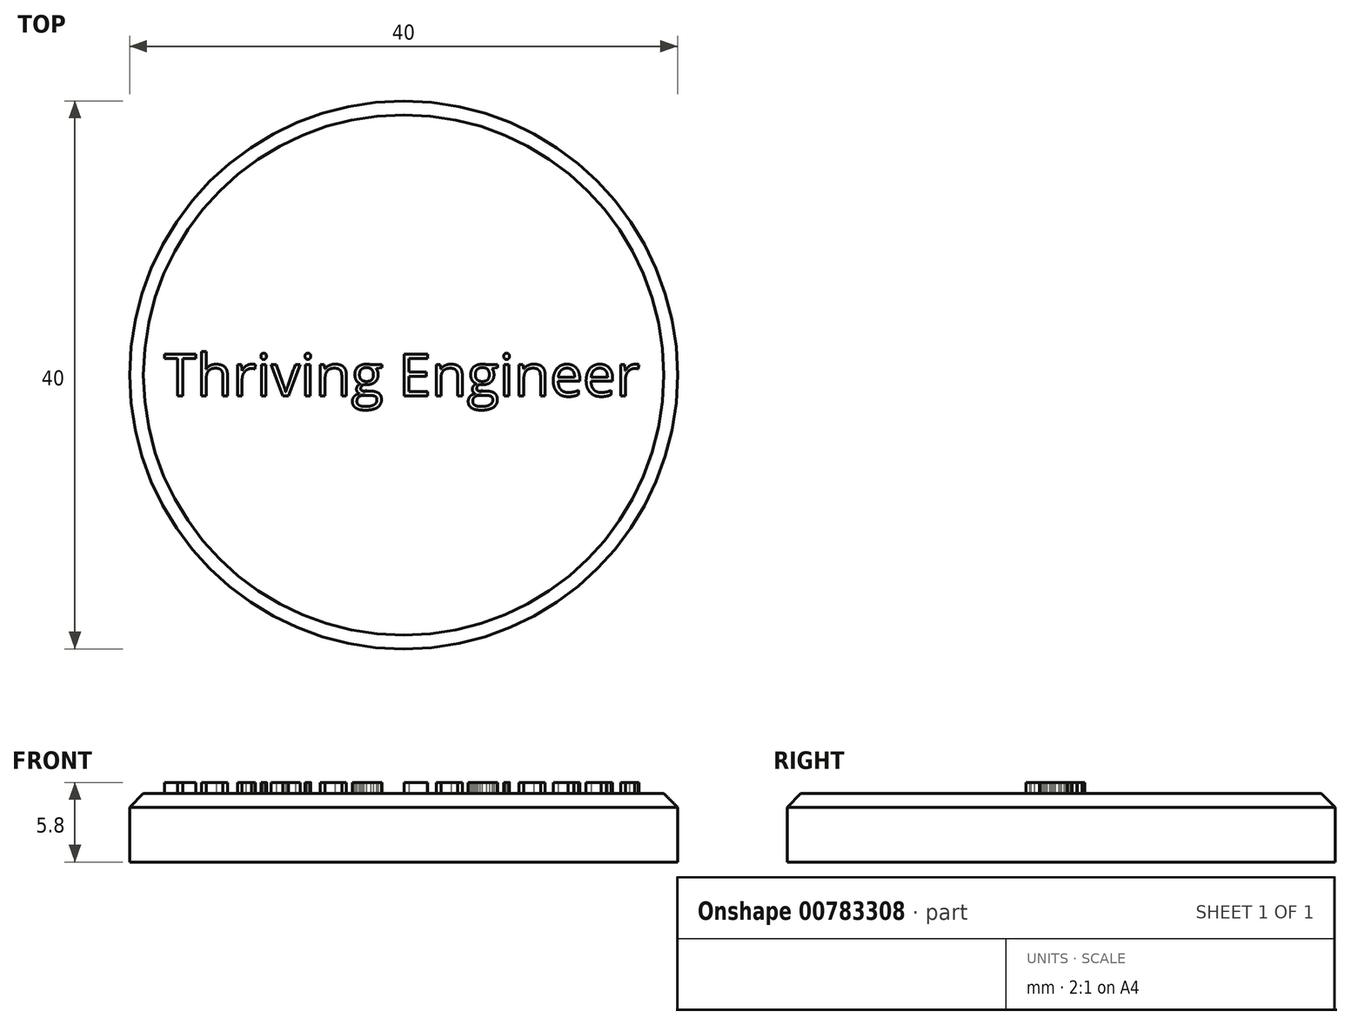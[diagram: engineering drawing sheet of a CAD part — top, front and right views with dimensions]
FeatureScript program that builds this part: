
annotation { "Feature Type Name" : "Feature", "Feature Type Description" : "" }
export const myFeature = defineFeature(function(context is Context, id is Id, definition is map)
    precondition{}
    {
        {
            var Q0;
            Q0=qCreatedBy(makeId("Top.planeOp"),FACE);
            var sketch = newSketch(context, id + "F0", { "sketchPlane" : qUnion([Q0])});
            skCircle(sketch, "E0", {"center": v(0, 0) * mm, "radius": 20 * mm});
            skLineSegment(sketch, "E1", {"start": v(-2.13, 19.89) * mm, "end": v(-1, 23) * mm});
            skLineSegment(sketch, "E2", {"start": v(-1, 23) * mm, "end": v(1, 23) * mm});
            skLineSegment(sketch, "E3", {"start": v(1, 23) * mm, "end": v(2.13, 19.89) * mm});
            skSolve(sketch);
        }
        {
            var Q0;
            {var subQ0=sQuery(id+"F0.wireOp",EDGE,"E0");var subQ1=makeQuery(id+"F0.imprint","INTERSECT",VERTEX,{"derivedFrom":[subQ0,sQuery(id+"F0.wireOp",EDGE,"E1")]});Q0=makeQuery(id+"F0.imprint","IMPRINT",FACE,{"disambiguationData":[TD([[makeQuery(id+"F0.imprint","IMPRINT",EDGE,{"disambiguationData":[TD([[subQ1,1.0]])],"derivedFrom":subQ0}),1.0]])]});}
            var Q1;
            {var subQ0=sQuery(id+"F0.wireOp",EDGE,"E1");Q1=makeQuery(id+"F0.imprint","IMPRINT",FACE,{"disambiguationData":[TD([[makeQuery(id+"F0.imprint","IMPRINT",EDGE,{"derivedFrom":subQ0}),-1.0]])]});}
            extrude(context, id + "F1", {"entities" : qUnion([Q0, Q1]), "depth" : 5 * mm, "offsetDistance" : 25 * mm});
        }
        {
            var Q0;
            Q0=makeQuery(id+"F1.opExtrude","SWEPT_BODY",BODY,{"disambiguationData":[OSD([sQuery(id+"F0.wireOp",EDGE,"E0"),sQuery(id+"F0.wireOp",EDGE,"E1"),sQuery(id+"F0.wireOp",EDGE,"E2"),sQuery(id+"F0.wireOp",EDGE,"E3")])]});
            var Q1;
            Q1=sQuery(id+"F0.wireOp",EDGE,"E0");
            circularPattern(context, id + "F2", {"operationType" : NewBodyOperationType.ADD, "entities" : qUnion([Q0]), "axis" : qUnion([Q1]), "angle" : 360 * degree, "instanceCount" : 18, "equalSpace" : true});
        }
        {
            var Q0;
            Q0=makeQuery(id+"F1.opExtrude","CAP_FACE",FACE,{"disambiguationData":[OSD([sQuery(id+"F0.wireOp",EDGE,"E0"),sQuery(id+"F0.wireOp",EDGE,"E1"),sQuery(id+"F0.wireOp",EDGE,"E2"),sQuery(id+"F0.wireOp",EDGE,"E3")])],"isStart":false});
            var sketch = newSketch(context, id + "F3", { "sketchPlane" : qUnion([Q0])});
            skText(sketch, "E4", { "text": "Thriving Engineer", "fontName": "OpenSans-Regular.ttf"});
            const initialGuessF3  = {"E4": [-0.0175, -0.00154, 1, 0, 0.00308]};
            skSetInitialGuess(sketch, initialGuessF3);
            skSolve(sketch);
        }
        {
            var Q0;
            Q0=qSketchRegion(id+"F3",true);
            extrude(context, id + "F4", {"entities" : qUnion([Q0]), "operationType" : NewBodyOperationType.ADD, "depth" : 0.8 * mm, "offsetDistance" : 25 * mm});
        }
        {
            var Q0;
            {var subQ1=sQuery(id+"F0.wireOp",EDGE,"E1");var subQ2=sQuery(id+"F0.wireOp",EDGE,"E0");Q0=makeQuery(id+"F2.boolean.opBoolean","SPLIT",EDGE,{"disambiguationData":[TD([makeQuery(id+"F2.opPattern","COPY",FACE,{"derivedFrom":makeQuery(id+"F1.opExtrude","SWEPT_FACE",FACE,{"disambiguationData":[OSD([subQ1])]}),"instanceName":"12"})])],"derivedFrom":makeQuery(id+"F1.opExtrude","CAP_EDGE",EDGE,{"disambiguationData":[OSD([subQ2])],"isStart":false})});}
            var Q1;
            Q1=makeQuery(id+"F2.opPattern","COPY",EDGE,{"derivedFrom":makeQuery(id+"F1.opExtrude","CAP_EDGE",EDGE,{"disambiguationData":[OSD([sQuery(id+"F0.wireOp",EDGE,"E1")])],"isStart":false}),"instanceName":"12"});
            var Q2;
            Q2=makeQuery(id+"F2.opPattern","COPY",EDGE,{"derivedFrom":makeQuery(id+"F1.opExtrude","CAP_EDGE",EDGE,{"disambiguationData":[OSD([sQuery(id+"F0.wireOp",EDGE,"E2")])],"isStart":false}),"instanceName":"12"});
            var Q3;
            Q3=makeQuery(id+"F2.opPattern","COPY",EDGE,{"derivedFrom":makeQuery(id+"F1.opExtrude","CAP_EDGE",EDGE,{"disambiguationData":[OSD([sQuery(id+"F0.wireOp",EDGE,"E3")])],"isStart":false}),"instanceName":"12"});
            var Q4;
            {var subQ1=sQuery(id+"F0.wireOp",EDGE,"E1");var subQ2=sQuery(id+"F0.wireOp",EDGE,"E0");Q4=makeQuery(id+"F2.boolean.opBoolean","SPLIT",EDGE,{"disambiguationData":[TD([makeQuery(id+"F2.opPattern","COPY",FACE,{"derivedFrom":makeQuery(id+"F1.opExtrude","SWEPT_FACE",FACE,{"disambiguationData":[OSD([subQ1])]}),"instanceName":"11"})])],"derivedFrom":makeQuery(id+"F1.opExtrude","CAP_EDGE",EDGE,{"disambiguationData":[OSD([subQ2])],"isStart":false})});}
            var Q5;
            Q5=makeQuery(id+"F2.opPattern","COPY",EDGE,{"derivedFrom":makeQuery(id+"F1.opExtrude","CAP_EDGE",EDGE,{"disambiguationData":[OSD([sQuery(id+"F0.wireOp",EDGE,"E1")])],"isStart":false}),"instanceName":"11"});
            var Q6;
            Q6=makeQuery(id+"F2.opPattern","COPY",EDGE,{"derivedFrom":makeQuery(id+"F1.opExtrude","CAP_EDGE",EDGE,{"disambiguationData":[OSD([sQuery(id+"F0.wireOp",EDGE,"E2")])],"isStart":false}),"instanceName":"11"});
            var Q7;
            Q7=makeQuery(id+"F2.opPattern","COPY",EDGE,{"derivedFrom":makeQuery(id+"F1.opExtrude","CAP_EDGE",EDGE,{"disambiguationData":[OSD([sQuery(id+"F0.wireOp",EDGE,"E3")])],"isStart":false}),"instanceName":"11"});
            var Q8;
            Q8=makeQuery(id+"F2.opPattern","COPY",EDGE,{"derivedFrom":makeQuery(id+"F1.opExtrude","CAP_EDGE",EDGE,{"disambiguationData":[OSD([sQuery(id+"F0.wireOp",EDGE,"E3")])],"isStart":false}),"instanceName":"13"});
            var Q9;
            Q9=makeQuery(id+"F2.opPattern","COPY",EDGE,{"derivedFrom":makeQuery(id+"F1.opExtrude","CAP_EDGE",EDGE,{"disambiguationData":[OSD([sQuery(id+"F0.wireOp",EDGE,"E2")])],"isStart":false}),"instanceName":"13"});
            var Q10;
            Q10=makeQuery(id+"F2.opPattern","COPY",EDGE,{"derivedFrom":makeQuery(id+"F1.opExtrude","CAP_EDGE",EDGE,{"disambiguationData":[OSD([sQuery(id+"F0.wireOp",EDGE,"E1")])],"isStart":false}),"instanceName":"13"});
            var Q11;
            {var subQ1=sQuery(id+"F0.wireOp",EDGE,"E1");var subQ2=sQuery(id+"F0.wireOp",EDGE,"E0");Q11=makeQuery(id+"F2.boolean.opBoolean","SPLIT",EDGE,{"disambiguationData":[TD([makeQuery(id+"F2.opPattern","COPY",FACE,{"derivedFrom":makeQuery(id+"F1.opExtrude","SWEPT_FACE",FACE,{"disambiguationData":[OSD([subQ1])]}),"instanceName":"13"})])],"derivedFrom":makeQuery(id+"F1.opExtrude","CAP_EDGE",EDGE,{"disambiguationData":[OSD([subQ2])],"isStart":false})});}
            var Q12;
            Q12=makeQuery(id+"F2.opPattern","COPY",EDGE,{"derivedFrom":makeQuery(id+"F1.opExtrude","CAP_EDGE",EDGE,{"disambiguationData":[OSD([sQuery(id+"F0.wireOp",EDGE,"E3")])],"isStart":false}),"instanceName":"14"});
            var Q13;
            Q13=makeQuery(id+"F2.opPattern","COPY",EDGE,{"derivedFrom":makeQuery(id+"F1.opExtrude","CAP_EDGE",EDGE,{"disambiguationData":[OSD([sQuery(id+"F0.wireOp",EDGE,"E2")])],"isStart":false}),"instanceName":"14"});
            var Q14;
            Q14=makeQuery(id+"F2.opPattern","COPY",EDGE,{"derivedFrom":makeQuery(id+"F1.opExtrude","CAP_EDGE",EDGE,{"disambiguationData":[OSD([sQuery(id+"F0.wireOp",EDGE,"E1")])],"isStart":false}),"instanceName":"14"});
            var Q15;
            {var subQ1=sQuery(id+"F0.wireOp",EDGE,"E1");var subQ2=sQuery(id+"F0.wireOp",EDGE,"E0");Q15=makeQuery(id+"F2.boolean.opBoolean","SPLIT",EDGE,{"disambiguationData":[TD([makeQuery(id+"F2.opPattern","COPY",FACE,{"derivedFrom":makeQuery(id+"F1.opExtrude","SWEPT_FACE",FACE,{"disambiguationData":[OSD([subQ1])]}),"instanceName":"14"})])],"derivedFrom":makeQuery(id+"F1.opExtrude","CAP_EDGE",EDGE,{"disambiguationData":[OSD([subQ2])],"isStart":false})});}
            var Q16;
            Q16=makeQuery(id+"F2.opPattern","COPY",EDGE,{"derivedFrom":makeQuery(id+"F1.opExtrude","CAP_EDGE",EDGE,{"disambiguationData":[OSD([sQuery(id+"F0.wireOp",EDGE,"E3")])],"isStart":false}),"instanceName":"15"});
            var Q17;
            Q17=makeQuery(id+"F2.opPattern","COPY",EDGE,{"derivedFrom":makeQuery(id+"F1.opExtrude","CAP_EDGE",EDGE,{"disambiguationData":[OSD([sQuery(id+"F0.wireOp",EDGE,"E2")])],"isStart":false}),"instanceName":"15"});
            var Q18;
            Q18=makeQuery(id+"F2.opPattern","COPY",EDGE,{"derivedFrom":makeQuery(id+"F1.opExtrude","CAP_EDGE",EDGE,{"disambiguationData":[OSD([sQuery(id+"F0.wireOp",EDGE,"E1")])],"isStart":false}),"instanceName":"15"});
            var Q19;
            {var subQ1=sQuery(id+"F0.wireOp",EDGE,"E1");var subQ2=sQuery(id+"F0.wireOp",EDGE,"E0");Q19=makeQuery(id+"F2.boolean.opBoolean","SPLIT",EDGE,{"disambiguationData":[TD([makeQuery(id+"F2.opPattern","COPY",FACE,{"derivedFrom":makeQuery(id+"F1.opExtrude","SWEPT_FACE",FACE,{"disambiguationData":[OSD([subQ1])]}),"instanceName":"15"})])],"derivedFrom":makeQuery(id+"F1.opExtrude","CAP_EDGE",EDGE,{"disambiguationData":[OSD([subQ2])],"isStart":false})});}
            var Q20;
            Q20=makeQuery(id+"F2.opPattern","COPY",EDGE,{"derivedFrom":makeQuery(id+"F1.opExtrude","CAP_EDGE",EDGE,{"disambiguationData":[OSD([sQuery(id+"F0.wireOp",EDGE,"E3")])],"isStart":false}),"instanceName":"16"});
            var Q21;
            Q21=makeQuery(id+"F2.opPattern","COPY",EDGE,{"derivedFrom":makeQuery(id+"F1.opExtrude","CAP_EDGE",EDGE,{"disambiguationData":[OSD([sQuery(id+"F0.wireOp",EDGE,"E2")])],"isStart":false}),"instanceName":"16"});
            var Q22;
            Q22=makeQuery(id+"F2.opPattern","COPY",EDGE,{"derivedFrom":makeQuery(id+"F1.opExtrude","CAP_EDGE",EDGE,{"disambiguationData":[OSD([sQuery(id+"F0.wireOp",EDGE,"E1")])],"isStart":false}),"instanceName":"16"});
            var Q23;
            {var subQ1=sQuery(id+"F0.wireOp",EDGE,"E1");var subQ2=sQuery(id+"F0.wireOp",EDGE,"E0");Q23=makeQuery(id+"F2.boolean.opBoolean","SPLIT",EDGE,{"disambiguationData":[TD([makeQuery(id+"F2.opPattern","COPY",FACE,{"derivedFrom":makeQuery(id+"F1.opExtrude","SWEPT_FACE",FACE,{"disambiguationData":[OSD([subQ1])]}),"instanceName":"16"})])],"derivedFrom":makeQuery(id+"F1.opExtrude","CAP_EDGE",EDGE,{"disambiguationData":[OSD([subQ2])],"isStart":false})});}
            var Q24;
            Q24=makeQuery(id+"F2.opPattern","COPY",EDGE,{"derivedFrom":makeQuery(id+"F1.opExtrude","CAP_EDGE",EDGE,{"disambiguationData":[OSD([sQuery(id+"F0.wireOp",EDGE,"E3")])],"isStart":false}),"instanceName":"17"});
            var Q25;
            Q25=makeQuery(id+"F2.opPattern","COPY",EDGE,{"derivedFrom":makeQuery(id+"F1.opExtrude","CAP_EDGE",EDGE,{"disambiguationData":[OSD([sQuery(id+"F0.wireOp",EDGE,"E1")])],"isStart":false}),"instanceName":"17"});
            var Q26;
            {var subQ0=sQuery(id+"F0.wireOp",EDGE,"E3");var subQ2=sQuery(id+"F0.wireOp",EDGE,"E0");Q26=makeQuery(id+"F2.boolean.opBoolean","SPLIT",EDGE,{"disambiguationData":[TD([makeQuery(id+"F1.opExtrude","SWEPT_FACE",FACE,{"disambiguationData":[OSD([subQ0])]})])],"derivedFrom":makeQuery(id+"F1.opExtrude","CAP_EDGE",EDGE,{"disambiguationData":[OSD([subQ2])],"isStart":false})});}
            var Q27;
            Q27=makeQuery(id+"F1.opExtrude","CAP_EDGE",EDGE,{"disambiguationData":[OSD([sQuery(id+"F0.wireOp",EDGE,"E3")])],"isStart":false});
            var Q28;
            Q28=makeQuery(id+"F1.opExtrude","CAP_EDGE",EDGE,{"disambiguationData":[OSD([sQuery(id+"F0.wireOp",EDGE,"E1")])],"isStart":false});
            var Q29;
            {var subQ1=sQuery(id+"F0.wireOp",EDGE,"E1");var subQ2=sQuery(id+"F0.wireOp",EDGE,"E0");Q29=makeQuery(id+"F2.boolean.opBoolean","SPLIT",EDGE,{"disambiguationData":[TD([makeQuery(id+"F1.opExtrude","SWEPT_FACE",FACE,{"disambiguationData":[OSD([subQ1])]})])],"derivedFrom":makeQuery(id+"F1.opExtrude","CAP_EDGE",EDGE,{"disambiguationData":[OSD([subQ2])],"isStart":false})});}
            var Q30;
            Q30=makeQuery(id+"F2.opPattern","COPY",EDGE,{"derivedFrom":makeQuery(id+"F1.opExtrude","CAP_EDGE",EDGE,{"disambiguationData":[OSD([sQuery(id+"F0.wireOp",EDGE,"E3")])],"isStart":false}),"instanceName":"1"});
            var Q31;
            Q31=makeQuery(id+"F2.opPattern","COPY",EDGE,{"derivedFrom":makeQuery(id+"F1.opExtrude","CAP_EDGE",EDGE,{"disambiguationData":[OSD([sQuery(id+"F0.wireOp",EDGE,"E1")])],"isStart":false}),"instanceName":"1"});
            var Q32;
            {var subQ1=sQuery(id+"F0.wireOp",EDGE,"E1");var subQ2=sQuery(id+"F0.wireOp",EDGE,"E0");Q32=makeQuery(id+"F2.boolean.opBoolean","SPLIT",EDGE,{"disambiguationData":[TD([makeQuery(id+"F2.opPattern","COPY",FACE,{"derivedFrom":makeQuery(id+"F1.opExtrude","SWEPT_FACE",FACE,{"disambiguationData":[OSD([subQ1])]}),"instanceName":"1"})])],"derivedFrom":makeQuery(id+"F1.opExtrude","CAP_EDGE",EDGE,{"disambiguationData":[OSD([subQ2])],"isStart":false})});}
            var Q33;
            Q33=makeQuery(id+"F2.opPattern","COPY",EDGE,{"derivedFrom":makeQuery(id+"F1.opExtrude","CAP_EDGE",EDGE,{"disambiguationData":[OSD([sQuery(id+"F0.wireOp",EDGE,"E3")])],"isStart":false}),"instanceName":"2"});
            var Q34;
            Q34=makeQuery(id+"F2.opPattern","COPY",EDGE,{"derivedFrom":makeQuery(id+"F1.opExtrude","CAP_EDGE",EDGE,{"disambiguationData":[OSD([sQuery(id+"F0.wireOp",EDGE,"E1")])],"isStart":false}),"instanceName":"2"});
            var Q35;
            {var subQ1=sQuery(id+"F0.wireOp",EDGE,"E1");var subQ2=sQuery(id+"F0.wireOp",EDGE,"E0");Q35=makeQuery(id+"F2.boolean.opBoolean","SPLIT",EDGE,{"disambiguationData":[TD([makeQuery(id+"F2.opPattern","COPY",FACE,{"derivedFrom":makeQuery(id+"F1.opExtrude","SWEPT_FACE",FACE,{"disambiguationData":[OSD([subQ1])]}),"instanceName":"2"})])],"derivedFrom":makeQuery(id+"F1.opExtrude","CAP_EDGE",EDGE,{"disambiguationData":[OSD([subQ2])],"isStart":false})});}
            var Q36;
            Q36=makeQuery(id+"F2.opPattern","COPY",EDGE,{"derivedFrom":makeQuery(id+"F1.opExtrude","CAP_EDGE",EDGE,{"disambiguationData":[OSD([sQuery(id+"F0.wireOp",EDGE,"E3")])],"isStart":false}),"instanceName":"3"});
            var Q37;
            Q37=makeQuery(id+"F2.opPattern","COPY",EDGE,{"derivedFrom":makeQuery(id+"F1.opExtrude","CAP_EDGE",EDGE,{"disambiguationData":[OSD([sQuery(id+"F0.wireOp",EDGE,"E1")])],"isStart":false}),"instanceName":"3"});
            var Q38;
            {var subQ1=sQuery(id+"F0.wireOp",EDGE,"E1");var subQ2=sQuery(id+"F0.wireOp",EDGE,"E0");Q38=makeQuery(id+"F2.boolean.opBoolean","SPLIT",EDGE,{"disambiguationData":[TD([makeQuery(id+"F2.opPattern","COPY",FACE,{"derivedFrom":makeQuery(id+"F1.opExtrude","SWEPT_FACE",FACE,{"disambiguationData":[OSD([subQ1])]}),"instanceName":"3"})])],"derivedFrom":makeQuery(id+"F1.opExtrude","CAP_EDGE",EDGE,{"disambiguationData":[OSD([subQ2])],"isStart":false})});}
            var Q39;
            Q39=makeQuery(id+"F2.opPattern","COPY",EDGE,{"derivedFrom":makeQuery(id+"F1.opExtrude","CAP_EDGE",EDGE,{"disambiguationData":[OSD([sQuery(id+"F0.wireOp",EDGE,"E3")])],"isStart":false}),"instanceName":"4"});
            var Q40;
            Q40=makeQuery(id+"F2.opPattern","COPY",EDGE,{"derivedFrom":makeQuery(id+"F1.opExtrude","CAP_EDGE",EDGE,{"disambiguationData":[OSD([sQuery(id+"F0.wireOp",EDGE,"E2")])],"isStart":false}),"instanceName":"4"});
            var Q41;
            Q41=makeQuery(id+"F2.opPattern","COPY",EDGE,{"derivedFrom":makeQuery(id+"F1.opExtrude","CAP_EDGE",EDGE,{"disambiguationData":[OSD([sQuery(id+"F0.wireOp",EDGE,"E1")])],"isStart":false}),"instanceName":"4"});
            var Q42;
            Q42=makeQuery(id+"F2.opPattern","COPY",EDGE,{"derivedFrom":makeQuery(id+"F1.opExtrude","CAP_EDGE",EDGE,{"disambiguationData":[OSD([sQuery(id+"F0.wireOp",EDGE,"E2")])],"isStart":false}),"instanceName":"3"});
            var Q43;
            Q43=makeQuery(id+"F2.opPattern","COPY",EDGE,{"derivedFrom":makeQuery(id+"F1.opExtrude","CAP_EDGE",EDGE,{"disambiguationData":[OSD([sQuery(id+"F0.wireOp",EDGE,"E2")])],"isStart":false}),"instanceName":"2"});
            var Q44;
            Q44=makeQuery(id+"F2.opPattern","COPY",EDGE,{"derivedFrom":makeQuery(id+"F1.opExtrude","CAP_EDGE",EDGE,{"disambiguationData":[OSD([sQuery(id+"F0.wireOp",EDGE,"E2")])],"isStart":false}),"instanceName":"1"});
            var Q45;
            Q45=makeQuery(id+"F1.opExtrude","CAP_EDGE",EDGE,{"disambiguationData":[OSD([sQuery(id+"F0.wireOp",EDGE,"E2")])],"isStart":false});
            var Q46;
            Q46=makeQuery(id+"F2.opPattern","COPY",EDGE,{"derivedFrom":makeQuery(id+"F1.opExtrude","CAP_EDGE",EDGE,{"disambiguationData":[OSD([sQuery(id+"F0.wireOp",EDGE,"E2")])],"isStart":false}),"instanceName":"17"});
            var Q47;
            {var subQ1=sQuery(id+"F0.wireOp",EDGE,"E1");var subQ2=sQuery(id+"F0.wireOp",EDGE,"E0");Q47=makeQuery(id+"F2.boolean.opBoolean","SPLIT",EDGE,{"disambiguationData":[TD([makeQuery(id+"F2.opPattern","COPY",FACE,{"derivedFrom":makeQuery(id+"F1.opExtrude","SWEPT_FACE",FACE,{"disambiguationData":[OSD([subQ1])]}),"instanceName":"4"})])],"derivedFrom":makeQuery(id+"F1.opExtrude","CAP_EDGE",EDGE,{"disambiguationData":[OSD([subQ2])],"isStart":false})});}
            var Q48;
            Q48=makeQuery(id+"F2.opPattern","COPY",EDGE,{"derivedFrom":makeQuery(id+"F1.opExtrude","CAP_EDGE",EDGE,{"disambiguationData":[OSD([sQuery(id+"F0.wireOp",EDGE,"E3")])],"isStart":false}),"instanceName":"5"});
            var Q49;
            Q49=makeQuery(id+"F2.opPattern","COPY",EDGE,{"derivedFrom":makeQuery(id+"F1.opExtrude","CAP_EDGE",EDGE,{"disambiguationData":[OSD([sQuery(id+"F0.wireOp",EDGE,"E2")])],"isStart":false}),"instanceName":"5"});
            var Q50;
            Q50=makeQuery(id+"F2.opPattern","COPY",EDGE,{"derivedFrom":makeQuery(id+"F1.opExtrude","CAP_EDGE",EDGE,{"disambiguationData":[OSD([sQuery(id+"F0.wireOp",EDGE,"E1")])],"isStart":false}),"instanceName":"5"});
            var Q51;
            {var subQ1=sQuery(id+"F0.wireOp",EDGE,"E1");var subQ2=sQuery(id+"F0.wireOp",EDGE,"E0");Q51=makeQuery(id+"F2.boolean.opBoolean","SPLIT",EDGE,{"disambiguationData":[TD([makeQuery(id+"F2.opPattern","COPY",FACE,{"derivedFrom":makeQuery(id+"F1.opExtrude","SWEPT_FACE",FACE,{"disambiguationData":[OSD([subQ1])]}),"instanceName":"5"})])],"derivedFrom":makeQuery(id+"F1.opExtrude","CAP_EDGE",EDGE,{"disambiguationData":[OSD([subQ2])],"isStart":false})});}
            var Q52;
            Q52=makeQuery(id+"F2.opPattern","COPY",EDGE,{"derivedFrom":makeQuery(id+"F1.opExtrude","CAP_EDGE",EDGE,{"disambiguationData":[OSD([sQuery(id+"F0.wireOp",EDGE,"E3")])],"isStart":false}),"instanceName":"6"});
            var Q53;
            Q53=makeQuery(id+"F2.opPattern","COPY",EDGE,{"derivedFrom":makeQuery(id+"F1.opExtrude","CAP_EDGE",EDGE,{"disambiguationData":[OSD([sQuery(id+"F0.wireOp",EDGE,"E2")])],"isStart":false}),"instanceName":"6"});
            var Q54;
            Q54=makeQuery(id+"F2.opPattern","COPY",EDGE,{"derivedFrom":makeQuery(id+"F1.opExtrude","CAP_EDGE",EDGE,{"disambiguationData":[OSD([sQuery(id+"F0.wireOp",EDGE,"E1")])],"isStart":false}),"instanceName":"6"});
            var Q55;
            {var subQ1=sQuery(id+"F0.wireOp",EDGE,"E1");var subQ2=sQuery(id+"F0.wireOp",EDGE,"E0");Q55=makeQuery(id+"F2.boolean.opBoolean","SPLIT",EDGE,{"disambiguationData":[TD([makeQuery(id+"F2.opPattern","COPY",FACE,{"derivedFrom":makeQuery(id+"F1.opExtrude","SWEPT_FACE",FACE,{"disambiguationData":[OSD([subQ1])]}),"instanceName":"6"})])],"derivedFrom":makeQuery(id+"F1.opExtrude","CAP_EDGE",EDGE,{"disambiguationData":[OSD([subQ2])],"isStart":false})});}
            var Q56;
            Q56=makeQuery(id+"F2.opPattern","COPY",EDGE,{"derivedFrom":makeQuery(id+"F1.opExtrude","CAP_EDGE",EDGE,{"disambiguationData":[OSD([sQuery(id+"F0.wireOp",EDGE,"E3")])],"isStart":false}),"instanceName":"7"});
            var Q57;
            Q57=makeQuery(id+"F2.opPattern","COPY",EDGE,{"derivedFrom":makeQuery(id+"F1.opExtrude","CAP_EDGE",EDGE,{"disambiguationData":[OSD([sQuery(id+"F0.wireOp",EDGE,"E2")])],"isStart":false}),"instanceName":"7"});
            var Q58;
            Q58=makeQuery(id+"F2.opPattern","COPY",EDGE,{"derivedFrom":makeQuery(id+"F1.opExtrude","CAP_EDGE",EDGE,{"disambiguationData":[OSD([sQuery(id+"F0.wireOp",EDGE,"E1")])],"isStart":false}),"instanceName":"7"});
            var Q59;
            {var subQ0=sQuery(id+"F0.wireOp",EDGE,"E1");var subQ2=sQuery(id+"F0.wireOp",EDGE,"E0");Q59=makeQuery(id+"F2.boolean.opBoolean","SPLIT",EDGE,{"disambiguationData":[TD([makeQuery(id+"F2.opPattern","COPY",FACE,{"derivedFrom":makeQuery(id+"F1.opExtrude","SWEPT_FACE",FACE,{"disambiguationData":[OSD([subQ0])]}),"instanceName":"7"})])],"derivedFrom":makeQuery(id+"F1.opExtrude","CAP_EDGE",EDGE,{"disambiguationData":[OSD([subQ2])],"isStart":false})});}
            var Q60;
            Q60=makeQuery(id+"F2.opPattern","COPY",EDGE,{"derivedFrom":makeQuery(id+"F1.opExtrude","CAP_EDGE",EDGE,{"disambiguationData":[OSD([sQuery(id+"F0.wireOp",EDGE,"E3")])],"isStart":false}),"instanceName":"8"});
            var Q61;
            Q61=makeQuery(id+"F2.opPattern","COPY",EDGE,{"derivedFrom":makeQuery(id+"F1.opExtrude","CAP_EDGE",EDGE,{"disambiguationData":[OSD([sQuery(id+"F0.wireOp",EDGE,"E2")])],"isStart":false}),"instanceName":"8"});
            var Q62;
            Q62=makeQuery(id+"F2.opPattern","COPY",EDGE,{"derivedFrom":makeQuery(id+"F1.opExtrude","CAP_EDGE",EDGE,{"disambiguationData":[OSD([sQuery(id+"F0.wireOp",EDGE,"E1")])],"isStart":false}),"instanceName":"8"});
            var Q63;
            {var subQ1=sQuery(id+"F0.wireOp",EDGE,"E1");var subQ2=sQuery(id+"F0.wireOp",EDGE,"E0");Q63=makeQuery(id+"F2.boolean.opBoolean","SPLIT",EDGE,{"disambiguationData":[TD([makeQuery(id+"F2.opPattern","COPY",FACE,{"derivedFrom":makeQuery(id+"F1.opExtrude","SWEPT_FACE",FACE,{"disambiguationData":[OSD([subQ1])]}),"instanceName":"8"})])],"derivedFrom":makeQuery(id+"F1.opExtrude","CAP_EDGE",EDGE,{"disambiguationData":[OSD([subQ2])],"isStart":false})});}
            var Q64;
            Q64=makeQuery(id+"F2.opPattern","COPY",EDGE,{"derivedFrom":makeQuery(id+"F1.opExtrude","CAP_EDGE",EDGE,{"disambiguationData":[OSD([sQuery(id+"F0.wireOp",EDGE,"E3")])],"isStart":false}),"instanceName":"9"});
            var Q65;
            Q65=makeQuery(id+"F2.opPattern","COPY",EDGE,{"derivedFrom":makeQuery(id+"F1.opExtrude","CAP_EDGE",EDGE,{"disambiguationData":[OSD([sQuery(id+"F0.wireOp",EDGE,"E2")])],"isStart":false}),"instanceName":"9"});
            var Q66;
            Q66=makeQuery(id+"F2.opPattern","COPY",EDGE,{"derivedFrom":makeQuery(id+"F1.opExtrude","CAP_EDGE",EDGE,{"disambiguationData":[OSD([sQuery(id+"F0.wireOp",EDGE,"E1")])],"isStart":false}),"instanceName":"9"});
            var Q67;
            {var subQ1=sQuery(id+"F0.wireOp",EDGE,"E1");var subQ2=sQuery(id+"F0.wireOp",EDGE,"E0");Q67=makeQuery(id+"F2.boolean.opBoolean","SPLIT",EDGE,{"disambiguationData":[TD([makeQuery(id+"F2.opPattern","COPY",FACE,{"derivedFrom":makeQuery(id+"F1.opExtrude","SWEPT_FACE",FACE,{"disambiguationData":[OSD([subQ1])]}),"instanceName":"9"})])],"derivedFrom":makeQuery(id+"F1.opExtrude","CAP_EDGE",EDGE,{"disambiguationData":[OSD([subQ2])],"isStart":false})});}
            var Q68;
            Q68=makeQuery(id+"F2.opPattern","COPY",EDGE,{"derivedFrom":makeQuery(id+"F1.opExtrude","CAP_EDGE",EDGE,{"disambiguationData":[OSD([sQuery(id+"F0.wireOp",EDGE,"E3")])],"isStart":false}),"instanceName":"10"});
            var Q69;
            Q69=makeQuery(id+"F2.opPattern","COPY",EDGE,{"derivedFrom":makeQuery(id+"F1.opExtrude","CAP_EDGE",EDGE,{"disambiguationData":[OSD([sQuery(id+"F0.wireOp",EDGE,"E2")])],"isStart":false}),"instanceName":"10"});
            var Q70;
            Q70=makeQuery(id+"F2.opPattern","COPY",EDGE,{"derivedFrom":makeQuery(id+"F1.opExtrude","CAP_EDGE",EDGE,{"disambiguationData":[OSD([sQuery(id+"F0.wireOp",EDGE,"E1")])],"isStart":false}),"instanceName":"10"});
            var Q71;
            {var subQ1=sQuery(id+"F0.wireOp",EDGE,"E1");var subQ2=sQuery(id+"F0.wireOp",EDGE,"E0");Q71=makeQuery(id+"F2.boolean.opBoolean","SPLIT",EDGE,{"disambiguationData":[TD([makeQuery(id+"F2.opPattern","COPY",FACE,{"derivedFrom":makeQuery(id+"F1.opExtrude","SWEPT_FACE",FACE,{"disambiguationData":[OSD([subQ1])]}),"instanceName":"10"})])],"derivedFrom":makeQuery(id+"F1.opExtrude","CAP_EDGE",EDGE,{"disambiguationData":[OSD([subQ2])],"isStart":false})});}
            chamfer(context, id + "F5", {"entities" : qUnion([Q0, Q1, Q2, Q3, Q4, Q5, Q6, Q7, Q8, Q9, Q10, Q11, Q12, Q13, Q14, Q15, Q16, Q17, Q18, Q19, Q20, Q21, Q22, Q23, Q24, Q25, Q26, Q27, Q28, Q29, Q30, Q31, Q32, Q33, Q34, Q35, Q36, Q37, Q38, Q39, Q40, Q41, Q42, Q43, Q44, Q45, Q46, Q47, Q48, Q49, Q50, Q51, Q52, Q53, Q54, Q55, Q56, Q57, Q58, Q59, Q60, Q61, Q62, Q63, Q64, Q65, Q66, Q67, Q68, Q69, Q70, Q71]), "width" : 1 * mm, "tangentPropagation" : true});
        }
    });
